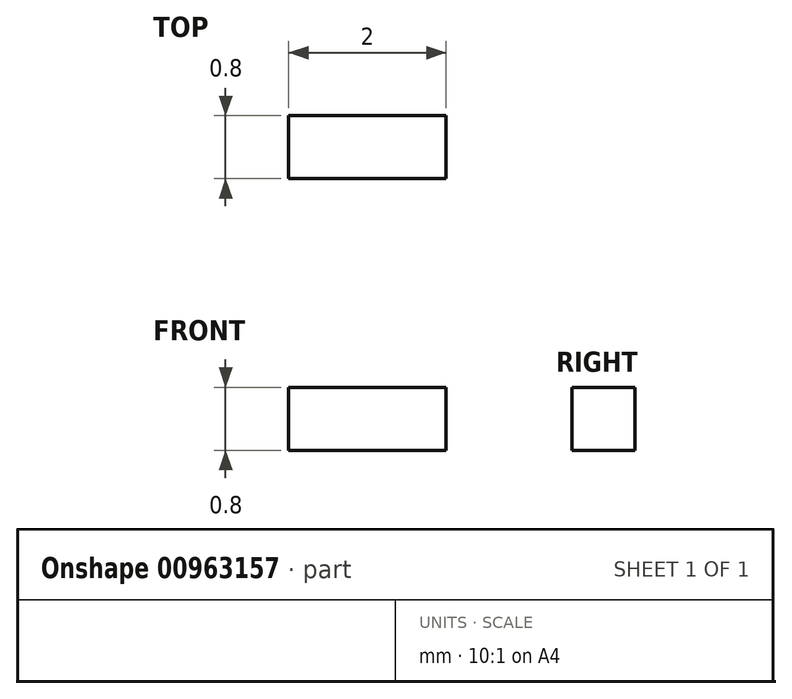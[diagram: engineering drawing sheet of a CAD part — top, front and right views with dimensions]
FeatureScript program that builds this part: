
annotation { "Feature Type Name" : "Feature", "Feature Type Description" : "" }
export const myFeature = defineFeature(function(context is Context, id is Id, definition is map)
    precondition{}
    {
        {
            var Q0;
            Q0=qCreatedBy(makeId("Front.planeOp"),FACE);
            var sketch = newSketch(context, id + "F0", { "sketchPlane" : qUnion([Q0])});
            skLineSegment(sketch, "E0", {"start": v(-5.88, -1.95) * mm, "end": v(-5.88, -2.75) * mm});
            skLineSegment(sketch, "E1", {"start": v(-5.88, -2.75) * mm, "end": v(-3.88, -2.75) * mm});
            skLineSegment(sketch, "E2", {"start": v(-3.88, -2.75) * mm, "end": v(-3.88, -1.95) * mm});
            skLineSegment(sketch, "E3", {"start": v(-3.88, -1.95) * mm, "end": v(-5.88, -1.95) * mm});
            skSolve(sketch);
        }
        {
            var Q0;
            Q0 = qSketchRegion(id + "F0", true);
            extrude(context, id + "F1", {"entities" : qUnion([Q0]), "depth" : 0.8 * mm, "offsetDistance" : 25 * mm});
        }
    });
